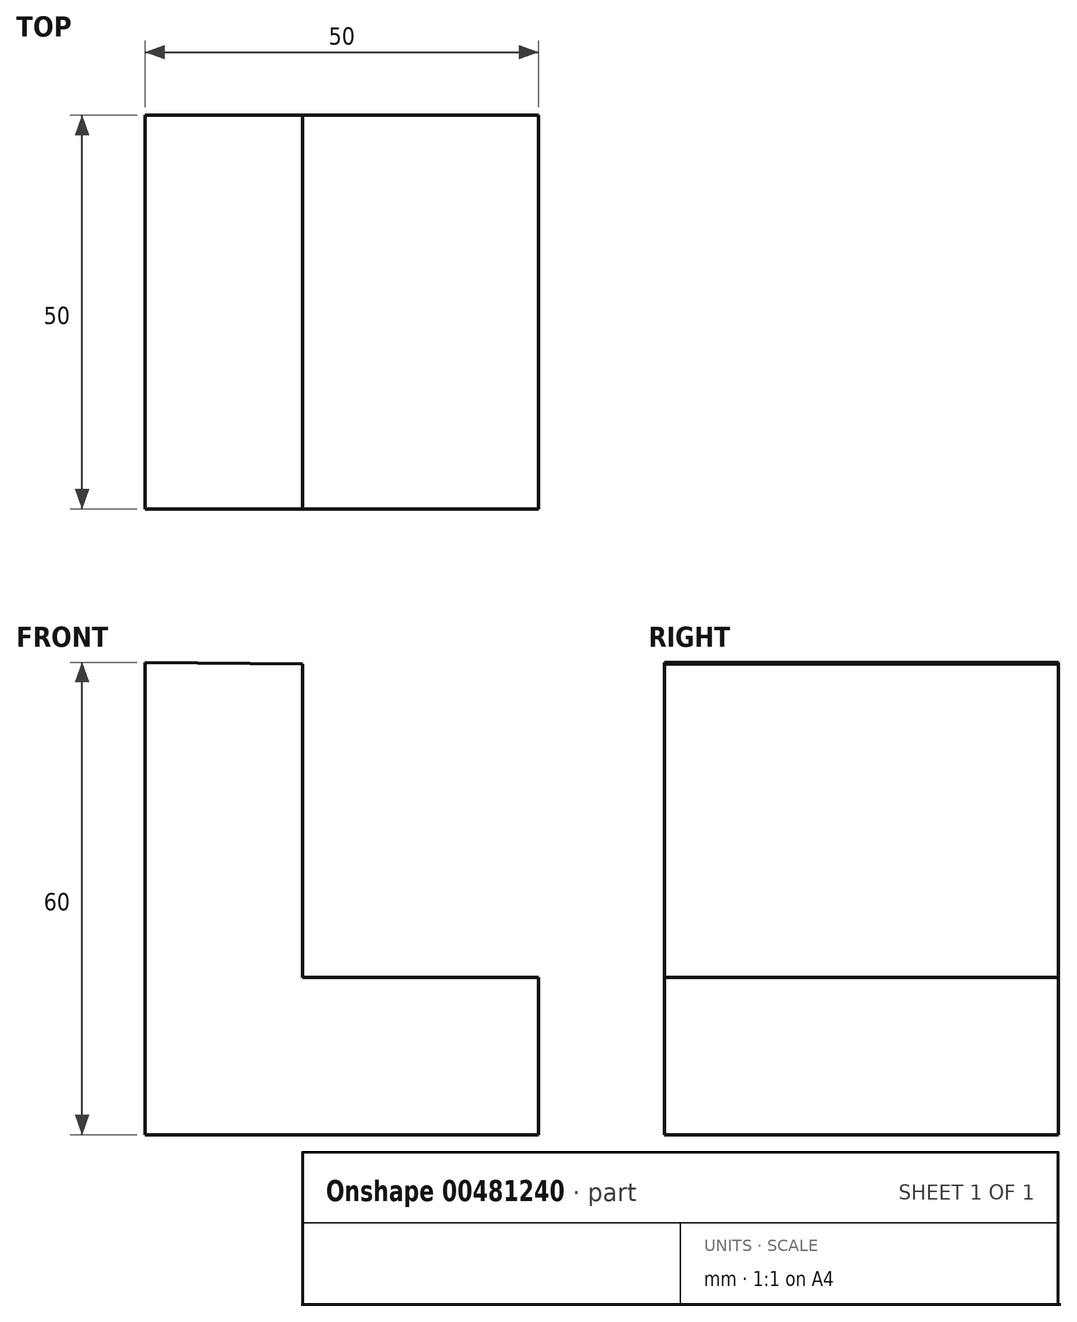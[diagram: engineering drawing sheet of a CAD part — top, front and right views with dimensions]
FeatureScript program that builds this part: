
annotation { "Feature Type Name" : "Feature", "Feature Type Description" : "" }
export const myFeature = defineFeature(function(context is Context, id is Id, definition is map)
    precondition{}
    {
        {
            var Q0;
            Q0=qCreatedBy(makeId("Front.planeOp"),FACE);
            var sketch = newSketch(context, id + "F0", { "sketchPlane" : qUnion([Q0])});
            skLineSegment(sketch, "E0", {"start": v(0, 0) * mm, "end": v(0, 60) * mm});
            skLineSegment(sketch, "E1", {"start": v(0, 60) * mm, "end": v(20, 59.78) * mm});
            skLineSegment(sketch, "E2", {"start": v(20, 59.78) * mm, "end": v(20, 20) * mm});
            skLineSegment(sketch, "E3", {"start": v(20, 20) * mm, "end": v(50, 20) * mm});
            skLineSegment(sketch, "E4", {"start": v(50, 20) * mm, "end": v(50, 0) * mm});
            skLineSegment(sketch, "E5", {"start": v(50, 0) * mm, "end": v(0, 0) * mm});
            skSolve(sketch);
        }
        {
            var Q0;
            Q0=makeQuery(id+"F0.imprint","IMPRINT",FACE,{"disambiguationData":[TD([[makeQuery(id+"F0.imprint","IMPRINT",EDGE,{"derivedFrom":sQuery(id+"F0.wireOp",EDGE,"E0")}),-1.0]])]});
            extrude(context, id + "F1", {"entities" : qUnion([Q0]), "depth" : 50 * mm});
        }
    });
